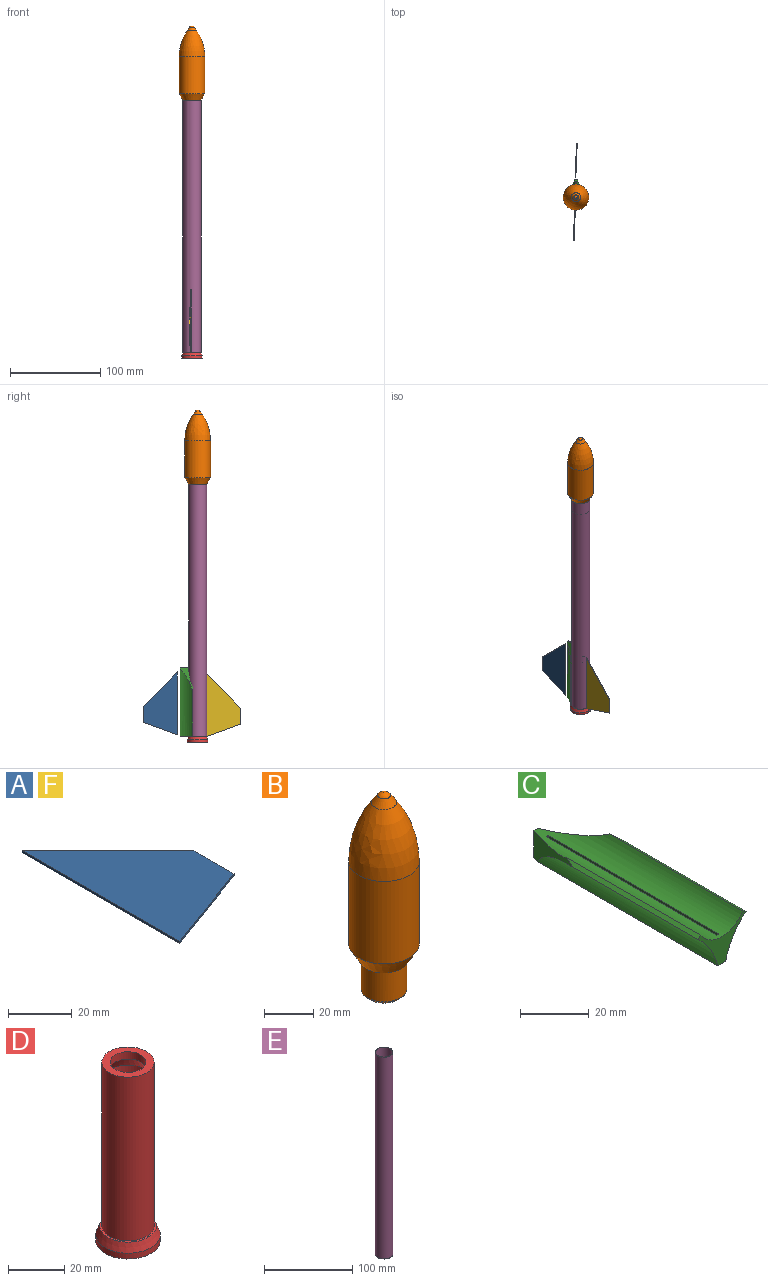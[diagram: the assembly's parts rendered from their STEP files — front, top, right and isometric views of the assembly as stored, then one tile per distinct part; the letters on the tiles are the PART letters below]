
ASSEMBLY  parts=6 mates=7
PART A: 6 faces, bbox 38.1x69.9x0.8 mm
  f0: plane 69.85x0.79mm, normal (-1,0,0), area 55.4mm2, adj f1,f3,f4,f5
  f1: plane 38.1x13.87mm, normal (0.34,-0.94,0), area 32.2mm2, adj f0,f2,f4,f5
  f2: plane 17.88x0.79mm, normal (1,0,0), area 14.2mm2, adj f1,f3,f4,f5
  f3: plane 38.1x38.1mm, normal (0.71,0.71,0), area 42.8mm2, adj f0,f2,f4,f5
  f4: plane 69.85x38.1mm, normal (0,0,1), area 1671.3mm2, adj f0,f1,f2,f3
  f5: plane 69.85x38.1mm, normal (0,0,-1), area 1671.3mm2, adj f0,f1,f2,f3
PART B: 19 faces, bbox 28.6x28.6x98.8 mm
  f0: sphere r=3.17mm, area 27mm2, adj f8
  f1: plane 16x16mm, normal (0,0,-1), area 201.1mm2, adj f2
  f2: cone r=8mm half-angle=45deg, axis (0,0,1), area 79.3mm2, adj f1,f9
  f3: cylinder r=9.27mm len=18.54mm, axis (0,0,-1), area 832.4mm2, adj f4,f9
  f4: cone r=9.27mm half-angle=60deg, axis (0,0,1), area 44.2mm2, adj f3,f5
  f5: cone r=9.91mm half-angle=30deg, axis (0,0,1), area 666mm2, adj f4,f6
  f6: cylinder r=14.29mm len=40.9mm, axis (0,0,-1), area 3671.6mm2, adj f5,f7
  f7: revolved ~29.14x28.58mm, area 2181.1mm2, adj f6,f8
  f8: cone r=5.1mm half-angle=35deg, axis (0,0,-1), area 105.4mm2, adj f0,f7
  f9: torus R=8.51mm, axis (0,0,1), area 34.6mm2, adj f2,f3
  f10: sphere r=2.54mm, area 17.3mm2, adj f11
  f11: cone r=4.58mm half-angle=35deg, axis (0,0,-1), area 91.2mm2, adj f10,f12
  f12: revolved ~28.77x27.31mm, area 2039.1mm2, adj f11,f13
  f13: cylinder r=13.65mm len=40.73mm, axis (0,0,-1), area 3493.8mm2, adj f12,f14
  f14: cone r=9.44mm half-angle=30deg, axis (0,0,1), area 611.1mm2, adj f13,f15
  f15: cone r=9.44mm half-angle=60deg, axis (0,0,1), area 52.8mm2, adj f14,f16
  f16: cylinder r=8.64mm len=17.27mm, axis (0,0,-1), area 798.1mm2, adj f15,f17
  f17: cone r=8.37mm half-angle=45deg, axis (0,0,1), area 19.9mm2, adj f16,f18
  f18: plane 16.75x16.75mm, normal (0,0,1), area 220.2mm2, adj f17
PART C: 14 faces, bbox 19.9x76.2x14.4 mm
  f0: plane 76.2x3.18mm, normal (0,0,-1), area 184.8mm2, adj f2,f4,f6,f7,f8,f9,f10,f11
  f1: cylinder r=10.03mm len=76.2mm, axis (0,1,0), area 1294.1mm2, adj f3,f4,f5,f7,f8,f9,f10,f11
  f2: cylinder r=25.4mm len=74.02mm, axis (0,1,0), area 1046.6mm2, adj f0,f3,f7,f12
  f3: plane 54.75x1.36mm, normal (0.52,0,0.86), area 84mm2, adj f1,f2,f7,f12
  f4: plane 9.56x1.59mm, normal (0,1,0), area 15.1mm2, adj f0,f1,f12,f13
  f5: plane 54.75x1.36mm, normal (-0.52,0,0.86), area 84mm2, adj f1,f6,f7,f13
  f6: cylinder r=25.4mm len=74.02mm, axis (0,1,0), area 1046.6mm2, adj f0,f5,f7,f13
  f7: plane 19.92x14.39mm, normal (0,-1,0), area 85.3mm2, adj f0,f1,f2,f3,f5,f6
  f8: plane 9.53x0.79mm, normal (0,1,0), area 7.6mm2, adj f0,f1,f9,f11
  f9: plane 69.85x9.53mm, normal (1,0,0), area 665.9mm2, adj f0,f1,f8,f10
  f10: plane 9.53x0.79mm, normal (0,-1,0), area 7.6mm2, adj f0,f1,f9,f11
  f11: plane 69.85x9.53mm, normal (-1,0,0), area 665.9mm2, adj f0,f1,f8,f10
  f12: plane 25.19x14.39mm, normal (0.94,0.34,0), area 102.5mm2, adj f0,f1,f2,f3,f4
  f13: plane 25.19x14.39mm, normal (-0.94,0.34,0), area 102.5mm2, adj f0,f1,f4,f5,f6
PART D: 9 faces, bbox 22.9x22.9x77.4 mm
  f0: cylinder r=11.43mm len=22.86mm, axis (0,0,-1), area 180.4mm2, adj f1,f8
  f1: cone r=10.03mm half-angle=20deg, axis (0,0,-1), area 275.4mm2, adj f0,f2
  f2: plane 20.07x20.07mm, normal (0,0,1), area 46.2mm2, adj f1,f3
  f3: cylinder r=9.27mm len=71.07mm, axis (0,0,-1), area 4140.2mm2, adj f2,f4
  f4: plane 18.54x18.54mm, normal (0,0,1), area 143.3mm2, adj f3,f5
  f5: cylinder r=6.35mm len=12.7mm, axis (0,0,-1), area 126.7mm2, adj f4,f6
  f6: cone r=6.35mm half-angle=30deg, axis (0,0,-1), area 243.2mm2, adj f5,f7
  f7: cylinder r=8.89mm len=69.85mm, axis (0,0,-1), area 3901.6mm2, adj f6,f8
  f8: plane 22.86x22.86mm, normal (0,0,-1), area 162.1mm2, adj f0,f7
PART E: 4 faces, bbox 20.1x20.1x279.4 mm
  f0: cylinder r=9.65mm len=279.4mm, axis (0,0,-1), area 16944.3mm2, adj f2,f3
  f1: cylinder r=10.03mm len=279.4mm, axis (0,0,-1), area 17613.2mm2, adj f2,f3
  f2: plane 20.07x20.07mm, normal (0,0,1), area 23.6mm2, adj f0,f1
  f3: plane 20.07x20.07mm, normal (0,0,-1), area 23.6mm2, adj f0,f1
PART F: same geometry as A
PLACE A rot(axis=(0.59,0.57,0.57),118.6deg) t=(-48.06,40.54,-70.48)mm
PLACE B t=(-47.02,17.94,207.7)mm
PLACE C rot(axis=(1,0,0),90deg) t=(-47.02,17.94,4.13)mm
PLACE D t=(-47.02,17.94,-78.42)mm
PLACE E t=(-47.02,17.94,-72.07)mm fixed
PLACE F rot(axis=(0.56,-0.59,-0.59),121.4deg) t=(-47.61,7.93,-72.48)mm
MATE slider C.f1 <-> E.f1  axis (0,0,1) through (-47.02,17.94,-33.97)mm
MATE slider D.f0 <-> E.f1  axis (0,0,-1) through (-47.02,17.94,-36.53)mm
MATE parallel F.f5 <-> A.f4  axis (1,-0.04,0) through (-48.26,-7.35,-42.41)mm
MATE planar C.f7 <-> E.f1  axis (0,0,-1) through (-47.02,30.4,-72.07)mm
MATE planar B.f2 <-> E.f0  axis (0,0,-1) through (-47.02,17.94,207.33)mm
MATE slider B.f2 <-> E.f1  axis (0,0,-1) through (-47.02,17.94,235.74)mm
MATE planar D.f0 <-> E.f1  axis (0,0,1) through (-47.02,17.94,-72.07)mm
